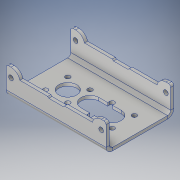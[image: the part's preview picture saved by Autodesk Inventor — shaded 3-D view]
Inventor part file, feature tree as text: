
AUTODESK INVENTOR PART (.ipt)
format: ipt  version: 2019 (Build 230136000, 136)  size: 223,744 bytes
history: native  units: in
note: dims shown in document units (in); Inventor stores cm internally (conversion verified against a paired STEP export)
features: sheet_metal_op x4, sketch x4, other x4, hole x2, projected_geometry x1
ambient origin geometry x8: Origin, YZ Plane, XZ Plane, XY Plane, X Axis, Y Axis, Z Axis, Center Point
bodies: Solid1 (feature_tree)
feature tree (15):
  sheet_metal_op  "Face1"
  sketch  "Sketch2"  dims[d2=0.0551in d3=0.5512in]
  hole  "Hole1"  [1 undecoded]
  sheet_metal_op  "Flange1"
  sketch  "Sketch4"  dims[d5=0.0827in d6=0.2362in d7=0.1575in d8=0.0787in d9=90.0deg d10=0.0551in d11=0.8108in d12=0.0551in d13=0.0in d14=0.0413in d15=0.0551in d16=0.0276in d17=0.1102in d18=0.0551in d19=0.4949in d20=90.0deg d21=0.0551in d22=0.2205in d23=0.0551in d24=0.0551in d26=0.3346in d27=1.5827in d28=0.0827in d29=0.2362in d30=0.1575in d31=0.0787in d32=90.0deg d33=0.0551in d34=0.8108in d35=0.0197in d36=0.0394in d37=0.2559in d38=135.0deg d39=0.0394in d40=0.0394in d41=0.0551in d42=0.0in]
  hole  "Hole2"  [1 undecoded]
  sketch  "Sketch1"  dims[d0=0.9681in d1=1.752in]
  other  "Plate1"
  sketch  "Sketch3"  dims[d4=0.315in]
  other  "Plate2"
  sheet_metal_op  "Bend1"
  sheet_metal_op  "Corner1"
  projected_geometry  "Projected Loop1"
  other  "Cut1"
  other  "Cut2"
note: 2 required parameter values undecoded (feature->parameter linkage not recoverable at this tier; creation-order binding heuristic only, values carry confidence <= 0.55)
